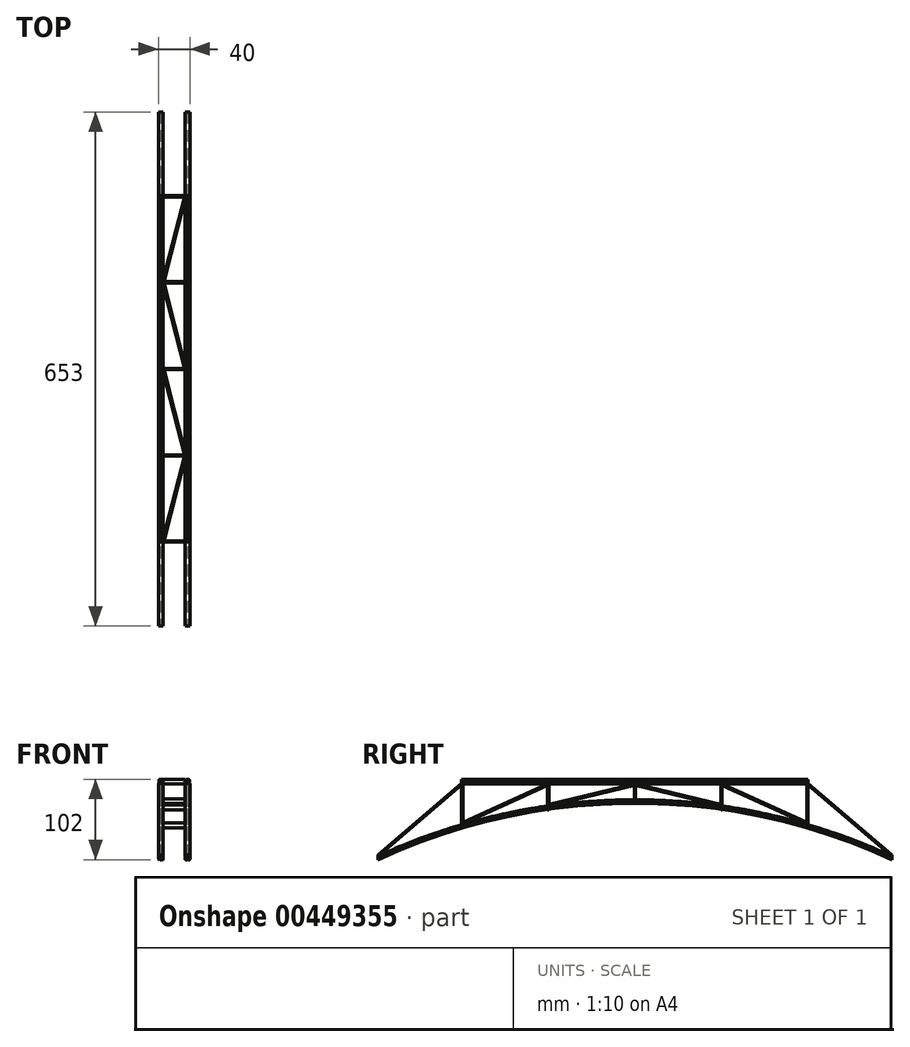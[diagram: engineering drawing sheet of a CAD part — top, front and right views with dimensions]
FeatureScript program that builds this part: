
annotation { "Feature Type Name" : "Feature", "Feature Type Description" : "" }
export const myFeature = defineFeature(function(context is Context, id is Id, definition is map)
    precondition{}
    {
        {
            var Q0;
            Q0=qCreatedBy(makeId("Front.planeOp"),FACE);
            var sketch = newSketch(context, id + "F0", { "sketchPlane" : qUnion([Q0])});
            skCircle(sketch, "E0", {"center": v(14.75, 0.75) * mm, "radius": 0.75 * mm});
            skCircle(sketch, "E1", {"center": v(16.25, 0.75) * mm, "radius": 0.75 * mm});
            skCircle(sketch, "E2", {"center": v(17.75, 0.75) * mm, "radius": 0.75 * mm});
            skCircle(sketch, "E3", {"center": v(19.25, 0.75) * mm, "radius": 0.75 * mm});
            skLineSegment(sketch, "E4", {"start": v(14.75, 0.75) * mm, "end": v(19.25, 0.75) * mm, "construction": true});
            skLineSegment(sketch, "E5", {"start": v(14.75, 0.75) * mm, "end": v(14, 0.75) * mm, "construction": true});
            skLineSegment(sketch, "E6", {"start": v(19.25, 0.75) * mm, "end": v(20, 0.75) * mm, "construction": true});
            skCircle(sketch, "E7.0.1.0", {"center": v(14.75, 2.25) * mm, "radius": 0.75 * mm});
            skCircle(sketch, "E7.0.1.1", {"center": v(16.25, 2.25) * mm, "radius": 0.75 * mm});
            skCircle(sketch, "E7.0.1.2", {"center": v(17.75, 2.25) * mm, "radius": 0.75 * mm});
            skCircle(sketch, "E7.0.1.3", {"center": v(19.25, 2.25) * mm, "radius": 0.75 * mm});
            skCircle(sketch, "E7.0.2.0", {"center": v(14.75, 3.75) * mm, "radius": 0.75 * mm});
            skCircle(sketch, "E7.0.2.1", {"center": v(16.25, 3.75) * mm, "radius": 0.75 * mm});
            skCircle(sketch, "E7.0.2.2", {"center": v(17.75, 3.75) * mm, "radius": 0.75 * mm});
            skCircle(sketch, "E7.0.2.3", {"center": v(19.25, 3.75) * mm, "radius": 0.75 * mm});
            skLineSegment(sketch, "E7.direction1", {"start": v(14.75, 0.75) * mm, "end": v(39.75, 0.75) * mm, "construction": true});
            skLineSegment(sketch, "E7.direction2", {"start": v(14.75, 0.75) * mm, "end": v(14.75, 2.25) * mm, "construction": true});
            skSolve(sketch);
        }
        {
            var Q0;
            Q0=qCreatedBy(makeId("Right.planeOp"),FACE);
            var sketch = newSketch(context, id + "F1", { "sketchPlane" : qUnion([Q0])});
            skArc(sketch, "E8", {"start": v(653, 0) * mm, "mid": v(326.5, 71.62) * mm, "end": v(0, 0) * mm});
            skLineSegment(sketch, "E9", {"start": v(653, 0) * mm, "end": v(0, 0) * mm, "construction": true});
            skLineSegment(sketch, "E10", {"start": v(326.5, 0) * mm, "end": v(326.5, 71.62) * mm, "construction": true});
            skSolve(sketch);
        }
        {
            var Q0;
            {var subQ0=sQuery(id+"F0.wireOp",EDGE,"E7.0.2.3");var subQ1=makeQuery(id+"F0.imprint","INTERSECT",VERTEX,{"derivedFrom":[sQuery(id+"F0.wireOp",EDGE,"E7.0.1.3"),subQ0]});Q0=makeQuery(id+"F0.imprint","IMPRINT",FACE,{"disambiguationData":[TD([[makeQuery(id+"F0.imprint","IMPRINT",EDGE,{"disambiguationData":[TD([[subQ1,1.0]])],"derivedFrom":subQ0}),1.0]])]});}
            var Q1;
            {var subQ0=sQuery(id+"F0.wireOp",EDGE,"E7.0.2.2");var subQ1=makeQuery(id+"F0.imprint","INTERSECT",VERTEX,{"derivedFrom":[sQuery(id+"F0.wireOp",EDGE,"E7.0.2.1"),subQ0]});Q1=makeQuery(id+"F0.imprint","IMPRINT",FACE,{"disambiguationData":[TD([[makeQuery(id+"F0.imprint","IMPRINT",EDGE,{"disambiguationData":[TD([[subQ1,1.0]])],"derivedFrom":subQ0}),1.0]])]});}
            var Q2;
            {var subQ0=sQuery(id+"F0.wireOp",EDGE,"E7.0.2.1");var subQ1=makeQuery(id+"F0.imprint","INTERSECT",VERTEX,{"derivedFrom":[sQuery(id+"F0.wireOp",EDGE,"E7.0.2.0"),subQ0]});Q2=makeQuery(id+"F0.imprint","IMPRINT",FACE,{"disambiguationData":[TD([[makeQuery(id+"F0.imprint","IMPRINT",EDGE,{"disambiguationData":[TD([[subQ1,1.0]])],"derivedFrom":subQ0}),1.0]])]});}
            var Q3;
            {var subQ0=sQuery(id+"F0.wireOp",EDGE,"E7.0.2.0");var subQ1=makeQuery(id+"F0.imprint","INTERSECT",VERTEX,{"derivedFrom":[sQuery(id+"F0.wireOp",EDGE,"E7.0.1.0"),subQ0]});Q3=makeQuery(id+"F0.imprint","IMPRINT",FACE,{"disambiguationData":[TD([[makeQuery(id+"F0.imprint","IMPRINT",EDGE,{"disambiguationData":[TD([[subQ1,1.0]])],"derivedFrom":subQ0}),1.0]])]});}
            var Q4;
            {var subQ0=sQuery(id+"F0.wireOp",EDGE,"E7.0.1.0");var subQ1=makeQuery(id+"F0.imprint","INTERSECT",VERTEX,{"derivedFrom":[subQ0,sQuery(id+"F0.wireOp",EDGE,"E7.0.2.0")]});Q4=makeQuery(id+"F0.imprint","IMPRINT",FACE,{"disambiguationData":[TD([[makeQuery(id+"F0.imprint","IMPRINT",EDGE,{"disambiguationData":[TD([[subQ1,1.0]])],"derivedFrom":subQ0}),1.0]])]});}
            var Q5;
            {var subQ0=sQuery(id+"F0.wireOp",EDGE,"E7.0.1.1");var subQ1=makeQuery(id+"F0.imprint","INTERSECT",VERTEX,{"derivedFrom":[subQ0,sQuery(id+"F0.wireOp",EDGE,"E7.0.2.1")]});Q5=makeQuery(id+"F0.imprint","IMPRINT",FACE,{"disambiguationData":[TD([[makeQuery(id+"F0.imprint","IMPRINT",EDGE,{"disambiguationData":[TD([[subQ1,1.0]])],"derivedFrom":subQ0}),1.0]])]});}
            var Q6;
            {var subQ0=sQuery(id+"F0.wireOp",EDGE,"E7.0.1.2");var subQ1=makeQuery(id+"F0.imprint","INTERSECT",VERTEX,{"derivedFrom":[subQ0,sQuery(id+"F0.wireOp",EDGE,"E7.0.2.2")]});Q6=makeQuery(id+"F0.imprint","IMPRINT",FACE,{"disambiguationData":[TD([[makeQuery(id+"F0.imprint","IMPRINT",EDGE,{"disambiguationData":[TD([[subQ1,1.0]])],"derivedFrom":subQ0}),1.0]])]});}
            var Q7;
            {var subQ0=sQuery(id+"F0.wireOp",EDGE,"E7.0.1.3");var subQ1=makeQuery(id+"F0.imprint","INTERSECT",VERTEX,{"derivedFrom":[subQ0,sQuery(id+"F0.wireOp",EDGE,"E7.0.2.3")]});Q7=makeQuery(id+"F0.imprint","IMPRINT",FACE,{"disambiguationData":[TD([[makeQuery(id+"F0.imprint","IMPRINT",EDGE,{"disambiguationData":[TD([[subQ1,-1.0]])],"derivedFrom":subQ0}),1.0]])]});}
            var Q8;
            {var subQ0=sQuery(id+"F0.wireOp",EDGE,"E3");var subQ1=makeQuery(id+"F0.imprint","INTERSECT",VERTEX,{"derivedFrom":[sQuery(id+"F0.wireOp",EDGE,"E2"),subQ0]});Q8=makeQuery(id+"F0.imprint","IMPRINT",FACE,{"disambiguationData":[TD([[makeQuery(id+"F0.imprint","IMPRINT",EDGE,{"disambiguationData":[TD([[subQ1,1.0]])],"derivedFrom":subQ0}),1.0]])]});}
            var Q9;
            {var subQ0=sQuery(id+"F0.wireOp",EDGE,"E2");var subQ1=makeQuery(id+"F0.imprint","INTERSECT",VERTEX,{"derivedFrom":[subQ0,sQuery(id+"F0.wireOp",EDGE,"E3")]});Q9=makeQuery(id+"F0.imprint","IMPRINT",FACE,{"disambiguationData":[TD([[makeQuery(id+"F0.imprint","IMPRINT",EDGE,{"disambiguationData":[TD([[subQ1,-1.0]])],"derivedFrom":subQ0}),1.0]])]});}
            var Q10;
            {var subQ0=sQuery(id+"F0.wireOp",EDGE,"E1");var subQ1=makeQuery(id+"F0.imprint","INTERSECT",VERTEX,{"derivedFrom":[subQ0,sQuery(id+"F0.wireOp",EDGE,"E2")]});Q10=makeQuery(id+"F0.imprint","IMPRINT",FACE,{"disambiguationData":[TD([[makeQuery(id+"F0.imprint","IMPRINT",EDGE,{"disambiguationData":[TD([[subQ1,-1.0]])],"derivedFrom":subQ0}),1.0]])]});}
            var Q11;
            {var subQ0=sQuery(id+"F0.wireOp",EDGE,"E0");var subQ1=makeQuery(id+"F0.imprint","INTERSECT",VERTEX,{"derivedFrom":[subQ0,sQuery(id+"F0.wireOp",EDGE,"E1")]});Q11=makeQuery(id+"F0.imprint","IMPRINT",FACE,{"disambiguationData":[TD([[makeQuery(id+"F0.imprint","IMPRINT",EDGE,{"disambiguationData":[TD([[subQ1,-1.0]])],"derivedFrom":subQ0}),1.0]])]});}
            var Q12;
            Q12=sQuery(id+"F1.wireOp",EDGE,"E8");
            sweep(context, id + "F2", {"profiles" : qUnion([Q0, Q1, Q2, Q3, Q4, Q5, Q6, Q7, Q8, Q9, Q10, Q11]), "path" : qUnion([Q12]), "keepProfileOrientation" : true});
        }
        {
            var Q0;
            Q0=makeQuery(id+"F2.opSweep","SWEPT_BODY",BODY,{"disambiguationData":[OSD([sQuery(id+"F0.wireOp",EDGE,"E7.0.2.3"),sQuery(id+"F1.wireOp",EDGE,"E8")])]});
            var Q1;
            Q1=makeQuery(id+"F2.opSweep","SWEPT_BODY",BODY,{"disambiguationData":[OSD([sQuery(id+"F0.wireOp",EDGE,"E7.0.2.2"),sQuery(id+"F1.wireOp",EDGE,"E8")])]});
            var Q2;
            Q2=makeQuery(id+"F2.opSweep","SWEPT_BODY",BODY,{"disambiguationData":[OSD([sQuery(id+"F0.wireOp",EDGE,"E7.0.2.1"),sQuery(id+"F1.wireOp",EDGE,"E8")])]});
            var Q3;
            Q3=makeQuery(id+"F2.opSweep","SWEPT_BODY",BODY,{"disambiguationData":[OSD([sQuery(id+"F0.wireOp",EDGE,"E7.0.2.0"),sQuery(id+"F1.wireOp",EDGE,"E8")])]});
            var Q4;
            Q4=makeQuery(id+"F2.opSweep","SWEPT_BODY",BODY,{"disambiguationData":[OSD([sQuery(id+"F0.wireOp",EDGE,"E7.0.1.0"),sQuery(id+"F1.wireOp",EDGE,"E8")])]});
            var Q5;
            Q5=makeQuery(id+"F2.opSweep","SWEPT_BODY",BODY,{"disambiguationData":[OSD([sQuery(id+"F0.wireOp",EDGE,"E7.0.1.1"),sQuery(id+"F1.wireOp",EDGE,"E8")])]});
            var Q6;
            Q6=makeQuery(id+"F2.opSweep","SWEPT_BODY",BODY,{"disambiguationData":[OSD([sQuery(id+"F0.wireOp",EDGE,"E7.0.1.2"),sQuery(id+"F1.wireOp",EDGE,"E8")])]});
            var Q7;
            Q7=makeQuery(id+"F2.opSweep","SWEPT_BODY",BODY,{"disambiguationData":[OSD([sQuery(id+"F0.wireOp",EDGE,"E7.0.1.3"),sQuery(id+"F1.wireOp",EDGE,"E8")])]});
            var Q8;
            Q8=makeQuery(id+"F2.opSweep","SWEPT_BODY",BODY,{"disambiguationData":[OSD([sQuery(id+"F0.wireOp",EDGE,"E3"),sQuery(id+"F1.wireOp",EDGE,"E8")])]});
            var Q9;
            Q9=makeQuery(id+"F2.opSweep","SWEPT_BODY",BODY,{"disambiguationData":[OSD([sQuery(id+"F0.wireOp",EDGE,"E2"),sQuery(id+"F1.wireOp",EDGE,"E8")])]});
            var Q10;
            Q10=makeQuery(id+"F2.opSweep","SWEPT_BODY",BODY,{"disambiguationData":[OSD([sQuery(id+"F0.wireOp",EDGE,"E1"),sQuery(id+"F1.wireOp",EDGE,"E8")])]});
            var Q11;
            Q11=makeQuery(id+"F2.opSweep","SWEPT_BODY",BODY,{"disambiguationData":[OSD([sQuery(id+"F0.wireOp",EDGE,"E0"),sQuery(id+"F1.wireOp",EDGE,"E8")])]});
            var Q12;
            Q12=qCreatedBy(makeId("Right.planeOp"),FACE);
            mirror(context, id + "F3", {"entities" : qUnion([Q0, Q1, Q2, Q3, Q4, Q5, Q6, Q7, Q8, Q9, Q10, Q11]), "mirrorPlane" : qUnion([Q12])});
        }
        {
            var Q0;
            Q0=qCreatedBy(makeId("Front.planeOp"),FACE);
            var sketch = newSketch(context, id + "F4", { "sketchPlane" : qUnion([Q0])});
            skCircle(sketch, "E11", {"center": v(15.5, 101.25) * mm, "radius": 0.75 * mm});
            skCircle(sketch, "E12", {"center": v(17, 101.25) * mm, "radius": 0.75 * mm});
            skCircle(sketch, "E13", {"center": v(18.5, 101.25) * mm, "radius": 0.75 * mm});
            skCircle(sketch, "E14.0.1.0", {"center": v(18.5, 99.75) * mm, "radius": 0.75 * mm});
            skCircle(sketch, "E14.0.1.1", {"center": v(17, 99.75) * mm, "radius": 0.75 * mm});
            skCircle(sketch, "E14.0.1.2", {"center": v(15.5, 99.75) * mm, "radius": 0.75 * mm});
            skCircle(sketch, "E14.0.2.0", {"center": v(18.5, 98.25) * mm, "radius": 0.75 * mm});
            skCircle(sketch, "E14.0.2.1", {"center": v(17, 98.25) * mm, "radius": 0.75 * mm});
            skCircle(sketch, "E14.0.2.2", {"center": v(15.5, 98.25) * mm, "radius": 0.75 * mm});
            skCircle(sketch, "E14.0.3.0", {"center": v(18.5, 96.75) * mm, "radius": 0.75 * mm});
            skCircle(sketch, "E14.0.3.1", {"center": v(17, 96.75) * mm, "radius": 0.75 * mm});
            skCircle(sketch, "E14.0.3.2", {"center": v(15.5, 96.75) * mm, "radius": 0.75 * mm});
            skLineSegment(sketch, "E14.direction1", {"start": v(18.5, 101.25) * mm, "end": v(43.5, 101.25) * mm, "construction": true});
            skLineSegment(sketch, "E14.direction2", {"start": v(18.5, 101.25) * mm, "end": v(18.5, 99.75) * mm, "construction": true});
            skCircle(sketch, "E15.0.0", {"center": v(16.25, 0.75) * mm, "radius": 0.75 * mm, "construction": true});
            skCircle(sketch, "E15.1.0", {"center": v(17.75, 0.75) * mm, "radius": 0.75 * mm, "construction": true});
            skLineSegment(sketch, "E16", {"start": v(16.25, 0.75) * mm, "end": v(17.75, 0.75) * mm, "construction": true});
            skCircle(sketch, "E17.1.0", {"center": v(16.25, 2.25) * mm, "radius": 0.75 * mm, "construction": true});
            skCircle(sketch, "E17.2.0", {"center": v(17.75, 2.25) * mm, "radius": 0.75 * mm, "construction": true});
            skLineSegment(sketch, "E18", {"start": v(16.25, 2.25) * mm, "end": v(17.75, 2.25) * mm, "construction": true});
            skLineSegment(sketch, "E19", {"start": v(17, 2.25) * mm, "end": v(17, 0.75) * mm, "construction": true});
            skLineSegment(sketch, "E20", {"start": v(17, 101.25) * mm, "end": v(17, 96.75) * mm, "construction": true});
            skSolve(sketch);
        }
        {
            var Q0;
            {var subQ0=sQuery(id+"F4.wireOp",EDGE,"E13");var subQ1=makeQuery(id+"F4.imprint","INTERSECT",VERTEX,{"derivedFrom":[sQuery(id+"F4.wireOp",EDGE,"E12"),subQ0]});Q0=makeQuery(id+"F4.imprint","IMPRINT",FACE,{"disambiguationData":[TD([[makeQuery(id+"F4.imprint","IMPRINT",EDGE,{"disambiguationData":[TD([[subQ1,-1.0]])],"derivedFrom":subQ0}),1.0]])]});}
            var Q1;
            {var subQ0=sQuery(id+"F4.wireOp",EDGE,"E12");var subQ1=makeQuery(id+"F4.imprint","INTERSECT",VERTEX,{"derivedFrom":[sQuery(id+"F4.wireOp",EDGE,"E11"),subQ0]});Q1=makeQuery(id+"F4.imprint","IMPRINT",FACE,{"disambiguationData":[TD([[makeQuery(id+"F4.imprint","IMPRINT",EDGE,{"disambiguationData":[TD([[subQ1,1.0]])],"derivedFrom":subQ0}),1.0]])]});}
            var Q2;
            {var subQ0=sQuery(id+"F4.wireOp",EDGE,"E11");var subQ1=makeQuery(id+"F4.imprint","INTERSECT",VERTEX,{"derivedFrom":[subQ0,sQuery(id+"F4.wireOp",EDGE,"E12")]});Q2=makeQuery(id+"F4.imprint","IMPRINT",FACE,{"disambiguationData":[TD([[makeQuery(id+"F4.imprint","IMPRINT",EDGE,{"disambiguationData":[TD([[subQ1,-1.0]])],"derivedFrom":subQ0}),1.0]])]});}
            var Q3;
            {var subQ0=sQuery(id+"F4.wireOp",EDGE,"E14.0.1.2");var subQ1=makeQuery(id+"F4.imprint","INTERSECT",VERTEX,{"derivedFrom":[sQuery(id+"F4.wireOp",EDGE,"E11"),subQ0]});Q3=makeQuery(id+"F4.imprint","IMPRINT",FACE,{"disambiguationData":[TD([[makeQuery(id+"F4.imprint","IMPRINT",EDGE,{"disambiguationData":[TD([[subQ1,1.0]])],"derivedFrom":subQ0}),1.0]])]});}
            var Q4;
            {var subQ0=sQuery(id+"F4.wireOp",EDGE,"E14.0.1.1");var subQ1=makeQuery(id+"F4.imprint","INTERSECT",VERTEX,{"derivedFrom":[sQuery(id+"F4.wireOp",EDGE,"E12"),subQ0]});Q4=makeQuery(id+"F4.imprint","IMPRINT",FACE,{"disambiguationData":[TD([[makeQuery(id+"F4.imprint","IMPRINT",EDGE,{"disambiguationData":[TD([[subQ1,1.0]])],"derivedFrom":subQ0}),1.0]])]});}
            var Q5;
            {var subQ0=sQuery(id+"F4.wireOp",EDGE,"E14.0.1.0");var subQ1=makeQuery(id+"F4.imprint","INTERSECT",VERTEX,{"derivedFrom":[sQuery(id+"F4.wireOp",EDGE,"E13"),subQ0]});Q5=makeQuery(id+"F4.imprint","IMPRINT",FACE,{"disambiguationData":[TD([[makeQuery(id+"F4.imprint","IMPRINT",EDGE,{"disambiguationData":[TD([[subQ1,-1.0]])],"derivedFrom":subQ0}),1.0]])]});}
            var Q6;
            {var subQ0=sQuery(id+"F4.wireOp",EDGE,"E14.0.2.0");var subQ1=makeQuery(id+"F4.imprint","INTERSECT",VERTEX,{"derivedFrom":[sQuery(id+"F4.wireOp",EDGE,"E14.0.1.0"),subQ0]});Q6=makeQuery(id+"F4.imprint","IMPRINT",FACE,{"disambiguationData":[TD([[makeQuery(id+"F4.imprint","IMPRINT",EDGE,{"disambiguationData":[TD([[subQ1,-1.0]])],"derivedFrom":subQ0}),1.0]])]});}
            var Q7;
            {var subQ0=sQuery(id+"F4.wireOp",EDGE,"E14.0.2.1");var subQ1=makeQuery(id+"F4.imprint","INTERSECT",VERTEX,{"derivedFrom":[sQuery(id+"F4.wireOp",EDGE,"E14.0.1.1"),subQ0]});Q7=makeQuery(id+"F4.imprint","IMPRINT",FACE,{"disambiguationData":[TD([[makeQuery(id+"F4.imprint","IMPRINT",EDGE,{"disambiguationData":[TD([[subQ1,1.0]])],"derivedFrom":subQ0}),1.0]])]});}
            var Q8;
            {var subQ0=sQuery(id+"F4.wireOp",EDGE,"E14.0.2.2");var subQ1=makeQuery(id+"F4.imprint","INTERSECT",VERTEX,{"derivedFrom":[sQuery(id+"F4.wireOp",EDGE,"E14.0.1.2"),subQ0]});Q8=makeQuery(id+"F4.imprint","IMPRINT",FACE,{"disambiguationData":[TD([[makeQuery(id+"F4.imprint","IMPRINT",EDGE,{"disambiguationData":[TD([[subQ1,1.0]])],"derivedFrom":subQ0}),1.0]])]});}
            var Q9;
            {var subQ0=sQuery(id+"F4.wireOp",EDGE,"E14.0.3.2");var subQ1=makeQuery(id+"F4.imprint","INTERSECT",VERTEX,{"derivedFrom":[sQuery(id+"F4.wireOp",EDGE,"E14.0.2.2"),subQ0]});Q9=makeQuery(id+"F4.imprint","IMPRINT",FACE,{"disambiguationData":[TD([[makeQuery(id+"F4.imprint","IMPRINT",EDGE,{"disambiguationData":[TD([[subQ1,1.0]])],"derivedFrom":subQ0}),1.0]])]});}
            var Q10;
            {var subQ0=sQuery(id+"F4.wireOp",EDGE,"E14.0.3.1");var subQ1=makeQuery(id+"F4.imprint","INTERSECT",VERTEX,{"derivedFrom":[sQuery(id+"F4.wireOp",EDGE,"E14.0.3.0"),subQ0]});Q10=makeQuery(id+"F4.imprint","IMPRINT",FACE,{"disambiguationData":[TD([[makeQuery(id+"F4.imprint","IMPRINT",EDGE,{"disambiguationData":[TD([[subQ1,-1.0]])],"derivedFrom":subQ0}),1.0]])]});}
            var Q11;
            {var subQ0=sQuery(id+"F4.wireOp",EDGE,"E14.0.3.0");var subQ1=makeQuery(id+"F4.imprint","INTERSECT",VERTEX,{"derivedFrom":[sQuery(id+"F4.wireOp",EDGE,"E14.0.2.0"),subQ0]});Q11=makeQuery(id+"F4.imprint","IMPRINT",FACE,{"disambiguationData":[TD([[makeQuery(id+"F4.imprint","IMPRINT",EDGE,{"disambiguationData":[TD([[subQ1,-1.0]])],"derivedFrom":subQ0}),1.0]])]});}
            extrude(context, id + "F5", {"entities" : qUnion([Q0, Q1, Q2, Q3, Q4, Q5, Q6, Q7, Q8, Q9, Q10, Q11]), "oppositeDirection" : true, "depth" : 653 * mm});
        }
        {
            var Q0;
            Q0=makeQuery(id+"F5.opExtrude","SWEPT_BODY",BODY,{"disambiguationData":[OSD([sQuery(id+"F4.wireOp",EDGE,"E11")])]});
            var Q1;
            Q1=makeQuery(id+"F5.opExtrude","SWEPT_BODY",BODY,{"disambiguationData":[OSD([sQuery(id+"F4.wireOp",EDGE,"E14.0.1.2")])]});
            var Q2;
            Q2=makeQuery(id+"F5.opExtrude","SWEPT_BODY",BODY,{"disambiguationData":[OSD([sQuery(id+"F4.wireOp",EDGE,"E14.0.2.2")])]});
            var Q3;
            Q3=makeQuery(id+"F5.opExtrude","SWEPT_BODY",BODY,{"disambiguationData":[OSD([sQuery(id+"F4.wireOp",EDGE,"E14.0.3.2")])]});
            var Q4;
            Q4=makeQuery(id+"F5.opExtrude","SWEPT_BODY",BODY,{"disambiguationData":[OSD([sQuery(id+"F4.wireOp",EDGE,"E14.0.3.1")])]});
            var Q5;
            Q5=makeQuery(id+"F5.opExtrude","SWEPT_BODY",BODY,{"disambiguationData":[OSD([sQuery(id+"F4.wireOp",EDGE,"E14.0.2.1")])]});
            var Q6;
            Q6=makeQuery(id+"F5.opExtrude","SWEPT_BODY",BODY,{"disambiguationData":[OSD([sQuery(id+"F4.wireOp",EDGE,"E14.0.1.1")])]});
            var Q7;
            Q7=makeQuery(id+"F5.opExtrude","SWEPT_BODY",BODY,{"disambiguationData":[OSD([sQuery(id+"F4.wireOp",EDGE,"E12")])]});
            var Q8;
            Q8=makeQuery(id+"F5.opExtrude","SWEPT_BODY",BODY,{"disambiguationData":[OSD([sQuery(id+"F4.wireOp",EDGE,"E13")])]});
            var Q9;
            Q9=makeQuery(id+"F5.opExtrude","SWEPT_BODY",BODY,{"disambiguationData":[OSD([sQuery(id+"F4.wireOp",EDGE,"E14.0.2.0")])]});
            var Q10;
            Q10=makeQuery(id+"F5.opExtrude","SWEPT_BODY",BODY,{"disambiguationData":[OSD([sQuery(id+"F4.wireOp",EDGE,"E14.0.3.0")])]});
            var Q11;
            Q11=makeQuery(id+"F5.opExtrude","SWEPT_BODY",BODY,{"disambiguationData":[OSD([sQuery(id+"F4.wireOp",EDGE,"E14.0.1.0")])]});
            var Q12;
            Q12=qCreatedBy(makeId("Right.planeOp"),FACE);
            mirror(context, id + "F6", {"entities" : qUnion([Q0, Q1, Q2, Q3, Q4, Q5, Q6, Q7, Q8, Q9, Q10, Q11]), "mirrorPlane" : qUnion([Q12])});
        }
        {
            var Q0;
            Q0=qCreatedBy(makeId("Top.planeOp"),FACE);
            cPlane(context, id + "F7", {"entities" : qUnion([Q0]), "cplaneType" : CPlaneType.OFFSET, "offset" : 102 * mm, "width" : 150 * mm, "height" : 150 * mm});
        }
        {
            var Q0;
            Q0=qCreatedBy(id+"F7.planeOp",FACE);
            var sketch = newSketch(context, id + "F8", { "sketchPlane" : qUnion([Q0])});
            skLineSegment(sketch, "E21", {"start": v(-17, 653) * mm, "end": v(17, 653) * mm, "construction": true});
            skLineSegment(sketch, "E22.0", {"start": v(17.75, 653) * mm, "end": v(16.25, 653) * mm, "construction": true});
            skLineSegment(sketch, "E22.1", {"start": v(-17.75, 653) * mm, "end": v(-16.25, 653) * mm, "construction": true});
            skLineSegment(sketch, "E23", {"start": v(0, 0) * mm, "end": v(0, 653) * mm, "construction": true});
            skLineSegment(sketch, "E24", {"start": v(-50, 326.5) * mm, "end": v(50, 326.5) * mm, "construction": true});
            skPoint(sketch, "E25", {"position": v(0, 326.5) * mm});
            skLineSegment(sketch, "E26.bottom", {"start": v(-50, 701.5) * mm, "end": v(50, 701.5) * mm});
            skLineSegment(sketch, "E26.top", {"start": v(-50, 546.5) * mm, "end": v(50, 546.5) * mm});
            skLineSegment(sketch, "E26.left", {"start": v(-50, 701.5) * mm, "end": v(-50, 546.5) * mm});
            skLineSegment(sketch, "E26.right", {"start": v(50, 701.5) * mm, "end": v(50, 546.5) * mm});
            skLineSegment(sketch, "E27.bottom", {"start": v(-50, 106.5) * mm, "end": v(50, 106.5) * mm});
            skLineSegment(sketch, "E27.top", {"start": v(-50, -48.5) * mm, "end": v(50, -48.5) * mm});
            skLineSegment(sketch, "E27.left", {"start": v(-50, 106.5) * mm, "end": v(-50, -48.5) * mm});
            skLineSegment(sketch, "E27.right", {"start": v(50, 106.5) * mm, "end": v(50, -48.5) * mm});
            skSolve(sketch);
        }
        {
            var Q0;
            Q0 = qSketchRegion(id + "F8", true);
            extrude(context, id + "F9", {"entities" : qUnion([Q0]), "operationType" : NewBodyOperationType.REMOVE, "oppositeDirection" : true, "depth" : 10 * mm});
        }
        {
            var Q0;
            Q0=qCreatedBy(id+"F7.planeOp",FACE);
            cPlane(context, id + "F10", {"entities" : qUnion([Q0]), "cplaneType" : CPlaneType.OFFSET, "offset" : 6 * mm, "oppositeDirection" : true, "width" : 150 * mm, "height" : 150 * mm});
        }
        {
            var Q0;
            Q0=qCreatedBy(id+"F10.planeOp",FACE);
            var sketch = newSketch(context, id + "F11", { "sketchPlane" : qUnion([Q0])});
            skLineSegment(sketch, "E28.0", {"start": v(-16.25, 546.5) * mm, "end": v(-14.75, 546.5) * mm, "construction": true});
            skLineSegment(sketch, "E28.1", {"start": v(14.75, 546.5) * mm, "end": v(16.25, 546.5) * mm, "construction": true});
            skLineSegment(sketch, "E28.2", {"start": v(14.75, 106.5) * mm, "end": v(16.25, 106.5) * mm, "construction": true});
            skLineSegment(sketch, "E28.3", {"start": v(-16.25, 106.5) * mm, "end": v(-14.75, 106.5) * mm, "construction": true});
            skLineSegment(sketch, "E29", {"start": v(-15.5, 546.5) * mm, "end": v(-15.5, 106.5) * mm, "construction": true});
            skLineSegment(sketch, "E30", {"start": v(15.5, 106.5) * mm, "end": v(15.5, 546.5) * mm, "construction": true});
            skLineSegment(sketch, "E31", {"start": v(-15.5, 326.5) * mm, "end": v(15.5, 326.5) * mm, "construction": true});
            skCircle(sketch, "E32", {"center": v(-16.25, 326.5) * mm, "radius": 0.75 * mm});
            skCircle(sketch, "E33", {"center": v(-14.75, 326.5) * mm, "radius": 0.75 * mm});
            skCircle(sketch, "E34", {"center": v(-17.75, 326.5) * mm, "radius": 0.75 * mm});
            skCircle(sketch, "E35", {"center": v(-19.25, 326.5) * mm, "radius": 0.75 * mm});
            skLineSegment(sketch, "E36.0", {"start": v(-17.75, 546.5) * mm, "end": v(-16.25, 546.5) * mm});
            skLineSegment(sketch, "E36.1", {"start": v(16.25, 546.5) * mm, "end": v(17.75, 546.5) * mm});
            skLineSegment(sketch, "E37", {"start": v(17, 546.5) * mm, "end": v(17, 106.5) * mm, "construction": true});
            skLineSegment(sketch, "E38", {"start": v(-17, 546.5) * mm, "end": v(-17, 106.5) * mm, "construction": true});
            skPoint(sketch, "E39", {"position": v(-17, 326.5) * mm});
            skLineSegment(sketch, "E40", {"start": v(-17.75, 326.5) * mm, "end": v(-16.25, 326.5) * mm, "construction": true});
            skSolve(sketch);
        }
        {
            var Q0;
            Q0 = qSketchRegion(id + "F11", true);
            extrude(context, id + "F12", {"entities" : qUnion([Q0]), "oppositeDirection" : true, "depth" : 20 * mm});
        }
        {
            var Q0;
            Q0=qCreatedBy(id+"F10.planeOp",FACE);
            var sketch = newSketch(context, id + "F13", { "sketchPlane" : qUnion([Q0])});
            skLineSegment(sketch, "E41.0", {"start": v(-17.75, 546.5) * mm, "end": v(-16.25, 546.5) * mm});
            skLineSegment(sketch, "E41.1", {"start": v(-17.75, 106.5) * mm, "end": v(-16.25, 106.5) * mm});
            skLineSegment(sketch, "E42", {"start": v(-17, 106.5) * mm, "end": v(-17, 546.5) * mm, "construction": true});
            skPoint(sketch, "E43", {"position": v(-17, 326.5) * mm});
            skPoint(sketch, "E44", {"position": v(-17, 436.5) * mm});
            skPoint(sketch, "E45", {"position": v(-17, 216.5) * mm});
            skCircle(sketch, "E46", {"center": v(-19.25, 216.5) * mm, "radius": 0.75 * mm});
            skCircle(sketch, "E47", {"center": v(-17.75, 216.5) * mm, "radius": 0.75 * mm});
            skCircle(sketch, "E48", {"center": v(-16.25, 216.5) * mm, "radius": 0.75 * mm});
            skCircle(sketch, "E49", {"center": v(-14.75, 216.5) * mm, "radius": 0.75 * mm});
            skCircle(sketch, "E50", {"center": v(-19.25, 436.5) * mm, "radius": 0.75 * mm});
            skCircle(sketch, "E51", {"center": v(-17.75, 436.5) * mm, "radius": 0.75 * mm});
            skCircle(sketch, "E52", {"center": v(-16.25, 436.5) * mm, "radius": 0.75 * mm});
            skCircle(sketch, "E53", {"center": v(-14.75, 436.5) * mm, "radius": 0.75 * mm});
            skLineSegment(sketch, "E54", {"start": v(-19.25, 436.5) * mm, "end": v(-14.75, 436.5) * mm, "construction": true});
            skLineSegment(sketch, "E55", {"start": v(-19.25, 216.5) * mm, "end": v(-14.75, 216.5) * mm, "construction": true});
            skSolve(sketch);
        }
        {
            var Q0;
            Q0 = qSketchRegion(id + "F13", true);
            extrude(context, id + "F14", {"entities" : qUnion([Q0]), "oppositeDirection" : true, "depth" : 27.5 * mm});
        }
        {
            var Q0;
            Q0=qCreatedBy(id+"F10.planeOp",FACE);
            var sketch = newSketch(context, id + "F15", { "sketchPlane" : qUnion([Q0])});
            skLineSegment(sketch, "E56.0", {"start": v(-17.75, 106.5) * mm, "end": v(-16.25, 106.5) * mm, "construction": true});
            skLineSegment(sketch, "E56.1", {"start": v(-17.75, 546.5) * mm, "end": v(-16.25, 546.5) * mm, "construction": true});
            skLineSegment(sketch, "E57", {"start": v(-17, 546.5) * mm, "end": v(-17, 106.5) * mm, "construction": true});
            skCircle(sketch, "E58", {"center": v(-19.25, 545.75) * mm, "radius": 0.75 * mm});
            skCircle(sketch, "E59", {"center": v(-17.75, 545.75) * mm, "radius": 0.75 * mm});
            skCircle(sketch, "E60", {"center": v(-16.25, 545.75) * mm, "radius": 0.75 * mm});
            skCircle(sketch, "E61", {"center": v(-14.75, 545.75) * mm, "radius": 0.75 * mm});
            skLineSegment(sketch, "E62", {"start": v(-19.25, 545.75) * mm, "end": v(-14.75, 545.75) * mm, "construction": true});
            skPoint(sketch, "E63", {"position": v(-17, 545.75) * mm});
            skLineSegment(sketch, "E64", {"start": v(-10.88, 326.5) * mm, "end": v(-17, 326.5) * mm});
            skCircle(sketch, "E65.MirrorC", {"center": v(-14.75, 107.25) * mm, "radius": 0.75 * mm});
            skCircle(sketch, "E66.MirrorC", {"center": v(-16.25, 107.25) * mm, "radius": 0.75 * mm});
            skCircle(sketch, "E67.MirrorC", {"center": v(-17.75, 107.25) * mm, "radius": 0.75 * mm});
            skCircle(sketch, "E68.MirrorC", {"center": v(-19.25, 107.25) * mm, "radius": 0.75 * mm});
            skSolve(sketch);
        }
        {
            var Q0;
            Q0 = qSketchRegion(id + "F15", true);
            extrude(context, id + "F16", {"entities" : qUnion([Q0]), "oppositeDirection" : true, "depth" : 50.5 * mm});
        }
        {
            var Q0;
            Q0=qCreatedBy(makeId("Right.planeOp"),FACE);
            cPlane(context, id + "F17", {"entities" : qUnion([Q0]), "cplaneType" : CPlaneType.OFFSET, "offset" : 20 * mm, "oppositeDirection" : true, "width" : 150 * mm, "height" : 150 * mm});
        }
        {
            var Q0;
            Q0=qCreatedBy(id+"F17.planeOp",FACE);
            var sketch = newSketch(context, id + "F18", { "sketchPlane" : qUnion([Q0])});
            skLineSegment(sketch, "E69", {"start": v(0, 5.25) * mm, "end": v(106.5, 96) * mm, "construction": true});
            skLineSegment(sketch, "E70.0", {"start": v(106.5, 97.5) * mm, "end": v(106.5, 96) * mm, "construction": true});
            skLineSegment(sketch, "E70.1", {"start": v(0, 3) * mm, "end": v(0, 4.5) * mm, "construction": true});
            skLineSegment(sketch, "E71.0", {"start": v(0, 4.26) * mm, "end": v(106.5, 95.01) * mm});
            skLineSegment(sketch, "E72.0", {"start": v(0, 6.24) * mm, "end": v(106.5, 96.98) * mm});
            skLineSegment(sketch, "E73", {"start": v(0, 6.24) * mm, "end": v(0, 4.26) * mm});
            skLineSegment(sketch, "E74", {"start": v(106.5, 96.98) * mm, "end": v(106.5, 95.01) * mm});
            skLineSegment(sketch, "E75.1", {"start": v(325.75, 76) * mm, "end": v(327.25, 76) * mm, "construction": true});
            skLineSegment(sketch, "E76.0", {"start": v(215.75, 96) * mm, "end": v(217.25, 96) * mm, "construction": true});
            skLineSegment(sketch, "E76.1", {"start": v(215.75, 68.5) * mm, "end": v(217.25, 68.5) * mm, "construction": true});
            skLineSegment(sketch, "E77.0", {"start": v(108, 45.5) * mm, "end": v(106.5, 45.5) * mm, "construction": true});
            skLineSegment(sketch, "E77.1", {"start": v(108, 96) * mm, "end": v(106.5, 96) * mm, "construction": true});
            skLineSegment(sketch, "E78", {"start": v(325.75, 95.23) * mm, "end": v(217.25, 69.27) * mm, "construction": true});
            skLineSegment(sketch, "E79", {"start": v(215.75, 95.18) * mm, "end": v(108, 46.32) * mm, "construction": true});
            skLineSegment(sketch, "E80.0", {"start": v(215.75, 96) * mm, "end": v(108, 47.15) * mm});
            skLineSegment(sketch, "E81.0", {"start": v(215.75, 94.35) * mm, "end": v(108, 45.5) * mm});
            skLineSegment(sketch, "E82.0", {"start": v(325.75, 96) * mm, "end": v(217.25, 70.04) * mm});
            skLineSegment(sketch, "E83.0", {"start": v(325.75, 94.46) * mm, "end": v(217.25, 68.5) * mm});
            skLineSegment(sketch, "E84.0", {"start": v(325.75, 96) * mm, "end": v(327.25, 96) * mm, "construction": true});
            skLineSegment(sketch, "E85", {"start": v(325.75, 96) * mm, "end": v(325.75, 94.46) * mm});
            skLineSegment(sketch, "E86", {"start": v(217.25, 68.5) * mm, "end": v(217.25, 70.04) * mm});
            skLineSegment(sketch, "E87", {"start": v(215.75, 96) * mm, "end": v(215.75, 94.35) * mm});
            skLineSegment(sketch, "E88", {"start": v(108, 47.15) * mm, "end": v(108, 45.5) * mm});
            skSolve(sketch);
        }
        {
            var Q0;
            Q0 = qSketchRegion(id + "F18", true);
            extrude(context, id + "F19", {"entities" : qUnion([Q0]), "depth" : 6 * mm});
        }
        {
            var Q0;
            Q0=makeQuery(id+"F9.boolean.opBoolean","COPY",FACE,{"disambiguationData":[TD([makeQuery(id+"F6.opPattern","COPY",FACE,{"derivedFrom":makeQuery(id+"F5.opExtrude","SWEPT_FACE",FACE,{"disambiguationData":[OSD([sQuery(id+"F4.wireOp",EDGE,"E13")])]}),"instanceName":"1"})])],"derivedFrom":makeQuery(id+"F9.opExtrude","SWEPT_FACE",FACE,{"disambiguationData":[OSD([sQuery(id+"F8.wireOp",EDGE,"E27.bottom")])]})});
            var Q1;
            Q1=makeQuery(id+"F9.boolean.opBoolean","COPY",FACE,{"disambiguationData":[TD([makeQuery(id+"F6.opPattern","COPY",FACE,{"derivedFrom":makeQuery(id+"F5.opExtrude","SWEPT_FACE",FACE,{"disambiguationData":[OSD([sQuery(id+"F4.wireOp",EDGE,"E13")])]}),"instanceName":"1"})])],"derivedFrom":makeQuery(id+"F9.opExtrude","SWEPT_FACE",FACE,{"disambiguationData":[OSD([sQuery(id+"F8.wireOp",EDGE,"E26.top")])]})});
            cPlane(context, id + "F20", {"entities" : qUnion([Q0, Q1]), "cplaneType" : CPlaneType.MID_PLANE, "offset" : 25 * mm, "width" : 150 * mm, "height" : 150 * mm});
        }
        {
            var Q0;
            Q0=makeQuery(id+"F19.opExtrude","SWEPT_BODY",BODY,{"disambiguationData":[OSD([sQuery(id+"F18.wireOp",EDGE,"E71.0"),sQuery(id+"F18.wireOp",EDGE,"E72.0"),sQuery(id+"F18.wireOp",EDGE,"E73"),sQuery(id+"F18.wireOp",EDGE,"E74")])]});
            var Q1;
            Q1=makeQuery(id+"F19.opExtrude","SWEPT_BODY",BODY,{"disambiguationData":[OSD([sQuery(id+"F18.wireOp",EDGE,"E80.0"),sQuery(id+"F18.wireOp",EDGE,"E81.0"),sQuery(id+"F18.wireOp",EDGE,"E87"),sQuery(id+"F18.wireOp",EDGE,"E88")])]});
            var Q2;
            Q2=makeQuery(id+"F19.opExtrude","SWEPT_BODY",BODY,{"disambiguationData":[OSD([sQuery(id+"F18.wireOp",EDGE,"E82.0"),sQuery(id+"F18.wireOp",EDGE,"E83.0"),sQuery(id+"F18.wireOp",EDGE,"E85"),sQuery(id+"F18.wireOp",EDGE,"E86")])]});
            var Q3;
            Q3=qCreatedBy(id+"F20.planeOp",FACE);
            mirror(context, id + "F21", {"entities" : qUnion([Q0, Q1, Q2]), "mirrorPlane" : qUnion([Q3])});
        }
        {
            var Q0;
            Q0=qCreatedBy(id+"F17.planeOp",FACE);
            cPlane(context, id + "F22", {"entities" : qUnion([Q0]), "cplaneType" : CPlaneType.OFFSET, "offset" : 6 * mm, "width" : 150 * mm, "height" : 150 * mm});
        }
        {
            var Q0;
            Q0=qCreatedBy(id+"F22.planeOp",FACE);
            var sketch = newSketch(context, id + "F23", { "sketchPlane" : qUnion([Q0])});
            skLineSegment(sketch, "E89.bottom", {"start": v(327.25, 77.5) * mm, "end": v(325.75, 77.5) * mm});
            skLineSegment(sketch, "E89.top", {"start": v(327.25, 71.5) * mm, "end": v(325.75, 71.5) * mm});
            skLineSegment(sketch, "E89.left", {"start": v(327.25, 77.5) * mm, "end": v(327.25, 71.5) * mm});
            skLineSegment(sketch, "E89.right", {"start": v(325.75, 77.5) * mm, "end": v(325.75, 71.5) * mm});
            skLineSegment(sketch, "E90.bottom", {"start": v(327.25, 102) * mm, "end": v(325.75, 102) * mm});
            skLineSegment(sketch, "E90.top", {"start": v(327.25, 96) * mm, "end": v(325.75, 96) * mm});
            skLineSegment(sketch, "E90.left", {"start": v(327.25, 102) * mm, "end": v(327.25, 96) * mm});
            skLineSegment(sketch, "E90.right", {"start": v(325.75, 102) * mm, "end": v(325.75, 96) * mm});
            skLineSegment(sketch, "E91.bottom", {"start": v(437.25, 102) * mm, "end": v(435.75, 102) * mm});
            skLineSegment(sketch, "E91.top", {"start": v(437.25, 96) * mm, "end": v(435.75, 96) * mm});
            skLineSegment(sketch, "E91.left", {"start": v(437.25, 102) * mm, "end": v(437.25, 96) * mm});
            skLineSegment(sketch, "E91.right", {"start": v(435.75, 102) * mm, "end": v(435.75, 96) * mm});
            skLineSegment(sketch, "E92.bottom", {"start": v(437.25, 69.5) * mm, "end": v(435.75, 69.5) * mm});
            skLineSegment(sketch, "E92.top", {"start": v(437.25, 63.5) * mm, "end": v(435.75, 63.5) * mm});
            skLineSegment(sketch, "E92.left", {"start": v(437.25, 69.5) * mm, "end": v(437.25, 63.5) * mm});
            skLineSegment(sketch, "E92.right", {"start": v(435.75, 69.5) * mm, "end": v(435.75, 63.5) * mm});
            skLineSegment(sketch, "E93.bottom", {"start": v(546.5, 46.5) * mm, "end": v(545, 46.5) * mm});
            skLineSegment(sketch, "E93.top", {"start": v(546.5, 40.5) * mm, "end": v(545, 40.5) * mm});
            skLineSegment(sketch, "E93.left", {"start": v(546.5, 46.5) * mm, "end": v(546.5, 40.5) * mm});
            skLineSegment(sketch, "E93.right", {"start": v(545, 46.5) * mm, "end": v(545, 40.5) * mm});
            skLineSegment(sketch, "E94.bottom", {"start": v(546.5, 102) * mm, "end": v(545, 102) * mm});
            skLineSegment(sketch, "E94.top", {"start": v(546.5, 96) * mm, "end": v(545, 96) * mm});
            skLineSegment(sketch, "E94.left", {"start": v(546.5, 102) * mm, "end": v(546.5, 96) * mm});
            skLineSegment(sketch, "E94.right", {"start": v(545, 102) * mm, "end": v(545, 96) * mm});
            skLineSegment(sketch, "E95.bottom", {"start": v(217.25, 102) * mm, "end": v(215.75, 102) * mm});
            skLineSegment(sketch, "E95.top", {"start": v(217.25, 96) * mm, "end": v(215.75, 96) * mm});
            skLineSegment(sketch, "E95.left", {"start": v(217.25, 102) * mm, "end": v(217.25, 96) * mm});
            skLineSegment(sketch, "E95.right", {"start": v(215.75, 102) * mm, "end": v(215.75, 96) * mm});
            skLineSegment(sketch, "E96.bottom", {"start": v(217.25, 69.5) * mm, "end": v(215.75, 69.5) * mm});
            skLineSegment(sketch, "E96.top", {"start": v(217.25, 63.5) * mm, "end": v(215.75, 63.5) * mm});
            skLineSegment(sketch, "E96.left", {"start": v(217.25, 69.5) * mm, "end": v(217.25, 63.5) * mm});
            skLineSegment(sketch, "E96.right", {"start": v(215.75, 69.5) * mm, "end": v(215.75, 63.5) * mm});
            skLineSegment(sketch, "E97.bottom", {"start": v(108, 46.5) * mm, "end": v(106.5, 46.5) * mm});
            skLineSegment(sketch, "E97.top", {"start": v(108, 40.5) * mm, "end": v(106.5, 40.5) * mm});
            skLineSegment(sketch, "E97.left", {"start": v(108, 46.5) * mm, "end": v(108, 40.5) * mm});
            skLineSegment(sketch, "E97.right", {"start": v(106.5, 46.5) * mm, "end": v(106.5, 40.5) * mm});
            skLineSegment(sketch, "E98.bottom", {"start": v(108, 102) * mm, "end": v(106.5, 102) * mm});
            skLineSegment(sketch, "E98.top", {"start": v(108, 96) * mm, "end": v(106.5, 96) * mm});
            skLineSegment(sketch, "E98.left", {"start": v(108, 102) * mm, "end": v(108, 96) * mm});
            skLineSegment(sketch, "E98.right", {"start": v(106.5, 102) * mm, "end": v(106.5, 96) * mm});
            skLineSegment(sketch, "E99.0", {"start": v(546.5, 102) * mm, "end": v(546.5, 100.5) * mm, "construction": true});
            skLineSegment(sketch, "E100.0", {"start": v(106.5, 102) * mm, "end": v(106.5, 100.5) * mm, "construction": true});
            skLineSegment(sketch, "E101.0", {"start": v(325.75, 96) * mm, "end": v(325.75, 94.46) * mm, "construction": true});
            skLineSegment(sketch, "E101.1", {"start": v(327.25, 96) * mm, "end": v(327.25, 94.46) * mm, "construction": true});
            skLineSegment(sketch, "E102", {"start": v(326.5, 102) * mm, "end": v(326.5, 96) * mm, "construction": true});
            skSolve(sketch);
        }
        {
            var Q0;
            Q0 = qSketchRegion(id + "F23", true);
            extrude(context, id + "F24", {"entities" : qUnion([Q0]), "depth" : 28 * mm});
        }
        {
            var Q0;
            Q0=qCreatedBy(id+"F7.planeOp",FACE);
            var sketch = newSketch(context, id + "F25", { "sketchPlane" : qUnion([Q0])});
            skLineSegment(sketch, "E103.0", {"start": v(14, 546.5) * mm, "end": v(14, 545) * mm});
            skLineSegment(sketch, "E103.1", {"start": v(-14, 437.25) * mm, "end": v(-14, 435.75) * mm});
            skLineSegment(sketch, "E103.2", {"start": v(14, 327.25) * mm, "end": v(14, 325.75) * mm});
            skLineSegment(sketch, "E103.3", {"start": v(-14, 327.25) * mm, "end": v(-14, 325.75) * mm});
            skLineSegment(sketch, "E103.4", {"start": v(14, 217.25) * mm, "end": v(14, 215.75) * mm});
            skLineSegment(sketch, "E103.5", {"start": v(-14, 108) * mm, "end": v(-14, 106.5) * mm, "construction": true});
            skLineSegment(sketch, "E104", {"start": v(-14, 108) * mm, "end": v(14, 215.75) * mm, "construction": true});
            skLineSegment(sketch, "E105", {"start": v(14, 217.25) * mm, "end": v(-14, 325.75) * mm, "construction": true});
            skLineSegment(sketch, "E106", {"start": v(14, 327.25) * mm, "end": v(-14, 435.75) * mm, "construction": true});
            skLineSegment(sketch, "E107", {"start": v(-14, 437.25) * mm, "end": v(14, 545) * mm, "construction": true});
            skLineSegment(sketch, "E108.0", {"start": v(-13.23, 437.25) * mm, "end": v(14, 542.02) * mm});
            skLineSegment(sketch, "E109.0", {"start": v(-14, 440.23) * mm, "end": v(13.23, 545) * mm});
            skLineSegment(sketch, "E110.0", {"start": v(14, 330.25) * mm, "end": v(-13.23, 435.75) * mm});
            skLineSegment(sketch, "E111.0", {"start": v(13.23, 327.25) * mm, "end": v(-14, 432.75) * mm});
            skLineSegment(sketch, "E112.0", {"start": v(14, 220.25) * mm, "end": v(-13.23, 325.75) * mm});
            skLineSegment(sketch, "E113.0", {"start": v(13.23, 217.25) * mm, "end": v(-14, 322.75) * mm});
            skLineSegment(sketch, "E114.0", {"start": v(-13.23, 108) * mm, "end": v(14, 212.77) * mm});
            skLineSegment(sketch, "E115.0", {"start": v(-14, 110.98) * mm, "end": v(13.23, 215.75) * mm});
            skLineSegment(sketch, "E116", {"start": v(-14, 110.98) * mm, "end": v(-14, 108) * mm});
            skLineSegment(sketch, "E117", {"start": v(-13.23, 108) * mm, "end": v(-14, 108) * mm});
            skLineSegment(sketch, "E118", {"start": v(13.23, 215.75) * mm, "end": v(14, 215.75) * mm});
            skLineSegment(sketch, "E119", {"start": v(14, 212.77) * mm, "end": v(14, 215.75) * mm});
            skLineSegment(sketch, "E120", {"start": v(13.23, 217.25) * mm, "end": v(14, 217.25) * mm});
            skLineSegment(sketch, "E121", {"start": v(14, 220.25) * mm, "end": v(14, 217.25) * mm});
            skLineSegment(sketch, "E122", {"start": v(-14, 322.75) * mm, "end": v(-14, 325.75) * mm});
            skLineSegment(sketch, "E123", {"start": v(-13.23, 325.75) * mm, "end": v(-14, 325.75) * mm});
            skLineSegment(sketch, "E124", {"start": v(13.23, 327.25) * mm, "end": v(14, 327.25) * mm});
            skLineSegment(sketch, "E125", {"start": v(14, 330.25) * mm, "end": v(14, 327.25) * mm});
            skLineSegment(sketch, "E126", {"start": v(-13.23, 435.75) * mm, "end": v(-14, 435.75) * mm});
            skLineSegment(sketch, "E127", {"start": v(-14, 432.75) * mm, "end": v(-14, 435.75) * mm});
            skLineSegment(sketch, "E128", {"start": v(-14, 440.23) * mm, "end": v(-14, 437.25) * mm});
            skLineSegment(sketch, "E129", {"start": v(-13.23, 437.25) * mm, "end": v(-14, 437.25) * mm});
            skLineSegment(sketch, "E130", {"start": v(13.23, 545) * mm, "end": v(14, 545) * mm});
            skLineSegment(sketch, "E131", {"start": v(14, 545) * mm, "end": v(14, 542.02) * mm});
            skSolve(sketch);
        }
        {
            var Q0;
            Q0 = qSketchRegion(id + "F25", true);
            extrude(context, id + "F26", {"entities" : qUnion([Q0]), "oppositeDirection" : true, "depth" : 6 * mm});
        }
        {
            var Q0;
            Q0=makeQuery(id+"F19.opExtrude","SWEPT_BODY",BODY,{"disambiguationData":[OSD([sQuery(id+"F18.wireOp",EDGE,"E71.0"),sQuery(id+"F18.wireOp",EDGE,"E72.0"),sQuery(id+"F18.wireOp",EDGE,"E73"),sQuery(id+"F18.wireOp",EDGE,"E74")])]});
            var Q1;
            Q1=makeQuery(id+"F19.opExtrude","SWEPT_BODY",BODY,{"disambiguationData":[OSD([sQuery(id+"F18.wireOp",EDGE,"E80.0"),sQuery(id+"F18.wireOp",EDGE,"E81.0"),sQuery(id+"F18.wireOp",EDGE,"E87"),sQuery(id+"F18.wireOp",EDGE,"E88")])]});
            var Q2;
            Q2=makeQuery(id+"F19.opExtrude","SWEPT_BODY",BODY,{"disambiguationData":[OSD([sQuery(id+"F18.wireOp",EDGE,"E82.0"),sQuery(id+"F18.wireOp",EDGE,"E83.0"),sQuery(id+"F18.wireOp",EDGE,"E85"),sQuery(id+"F18.wireOp",EDGE,"E86")])]});
            var Q3;
            Q3=makeQuery(id+"F21.opPattern","COPY",BODY,{"derivedFrom":makeQuery(id+"F19.opExtrude","SWEPT_BODY",BODY,{"disambiguationData":[OSD([sQuery(id+"F18.wireOp",EDGE,"E82.0"),sQuery(id+"F18.wireOp",EDGE,"E83.0"),sQuery(id+"F18.wireOp",EDGE,"E85"),sQuery(id+"F18.wireOp",EDGE,"E86")])]}),"instanceName":"1"});
            var Q4;
            Q4=makeQuery(id+"F21.opPattern","COPY",BODY,{"derivedFrom":makeQuery(id+"F19.opExtrude","SWEPT_BODY",BODY,{"disambiguationData":[OSD([sQuery(id+"F18.wireOp",EDGE,"E80.0"),sQuery(id+"F18.wireOp",EDGE,"E81.0"),sQuery(id+"F18.wireOp",EDGE,"E87"),sQuery(id+"F18.wireOp",EDGE,"E88")])]}),"instanceName":"1"});
            var Q5;
            Q5=makeQuery(id+"F21.opPattern","COPY",BODY,{"derivedFrom":makeQuery(id+"F19.opExtrude","SWEPT_BODY",BODY,{"disambiguationData":[OSD([sQuery(id+"F18.wireOp",EDGE,"E71.0"),sQuery(id+"F18.wireOp",EDGE,"E72.0"),sQuery(id+"F18.wireOp",EDGE,"E73"),sQuery(id+"F18.wireOp",EDGE,"E74")])]}),"instanceName":"1"});
            var Q6;
            Q6=makeQuery(id+"F14.opExtrude","SWEPT_BODY",BODY,{"disambiguationData":[OSD([sQuery(id+"F13.wireOp",EDGE,"E47")])]});
            var Q7;
            Q7=makeQuery(id+"F12.opExtrude","SWEPT_BODY",BODY,{"disambiguationData":[OSD([sQuery(id+"F11.wireOp",EDGE,"E32")])]});
            var Q8;
            Q8=makeQuery(id+"F12.opExtrude","SWEPT_BODY",BODY,{"disambiguationData":[OSD([sQuery(id+"F11.wireOp",EDGE,"E33")])]});
            var Q9;
            Q9=makeQuery(id+"F12.opExtrude","SWEPT_BODY",BODY,{"disambiguationData":[OSD([sQuery(id+"F11.wireOp",EDGE,"E34")])]});
            var Q10;
            Q10=makeQuery(id+"F12.opExtrude","SWEPT_BODY",BODY,{"disambiguationData":[OSD([sQuery(id+"F11.wireOp",EDGE,"E35")])]});
            var Q11;
            Q11=makeQuery(id+"F14.opExtrude","SWEPT_BODY",BODY,{"disambiguationData":[OSD([sQuery(id+"F13.wireOp",EDGE,"E49")])]});
            var Q12;
            Q12=makeQuery(id+"F14.opExtrude","SWEPT_BODY",BODY,{"disambiguationData":[OSD([sQuery(id+"F13.wireOp",EDGE,"E48")])]});
            var Q13;
            Q13=makeQuery(id+"F14.opExtrude","SWEPT_BODY",BODY,{"disambiguationData":[OSD([sQuery(id+"F13.wireOp",EDGE,"E46")])]});
            var Q14;
            Q14=makeQuery(id+"F16.opExtrude","SWEPT_BODY",BODY,{"disambiguationData":[OSD([sQuery(id+"F15.wireOp",EDGE,"E68.MirrorC")])]});
            var Q15;
            Q15=makeQuery(id+"F16.opExtrude","SWEPT_BODY",BODY,{"disambiguationData":[OSD([sQuery(id+"F15.wireOp",EDGE,"E65.MirrorC"),sQuery(id+"F15.wireOp",EDGE,"E66.MirrorC"),sQuery(id+"F15.wireOp",EDGE,"E67.MirrorC")])]});
            var Q16;
            Q16=makeQuery(id+"F14.opExtrude","SWEPT_BODY",BODY,{"disambiguationData":[OSD([sQuery(id+"F13.wireOp",EDGE,"E53")])]});
            var Q17;
            Q17=makeQuery(id+"F14.opExtrude","SWEPT_BODY",BODY,{"disambiguationData":[OSD([sQuery(id+"F13.wireOp",EDGE,"E52")])]});
            var Q18;
            Q18=makeQuery(id+"F14.opExtrude","SWEPT_BODY",BODY,{"disambiguationData":[OSD([sQuery(id+"F13.wireOp",EDGE,"E51")])]});
            var Q19;
            Q19=makeQuery(id+"F14.opExtrude","SWEPT_BODY",BODY,{"disambiguationData":[OSD([sQuery(id+"F13.wireOp",EDGE,"E50")])]});
            var Q20;
            Q20=makeQuery(id+"F16.opExtrude","SWEPT_BODY",BODY,{"disambiguationData":[OSD([sQuery(id+"F15.wireOp",EDGE,"E58")])]});
            var Q21;
            Q21=makeQuery(id+"F16.opExtrude","SWEPT_BODY",BODY,{"disambiguationData":[OSD([sQuery(id+"F15.wireOp",EDGE,"E59"),sQuery(id+"F15.wireOp",EDGE,"E60"),sQuery(id+"F15.wireOp",EDGE,"E61")])]});
            var Q22;
            Q22=qCreatedBy(makeId("Right.planeOp"),FACE);
            mirror(context, id + "F27", {"entities" : qUnion([Q0, Q1, Q2, Q3, Q4, Q5, Q6, Q7, Q8, Q9, Q10, Q11, Q12, Q13, Q14, Q15, Q16, Q17, Q18, Q19, Q20, Q21]), "mirrorPlane" : qUnion([Q22])});
        }
    });
